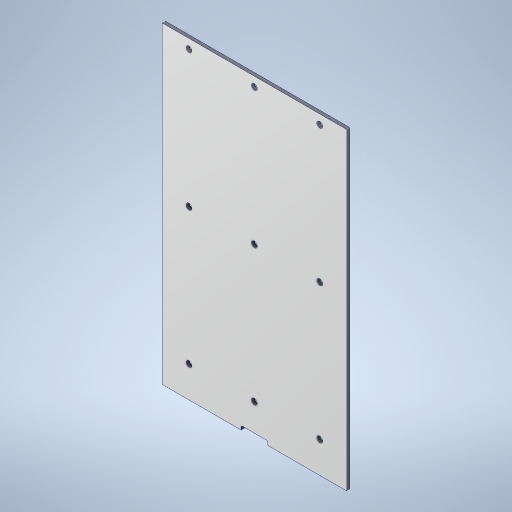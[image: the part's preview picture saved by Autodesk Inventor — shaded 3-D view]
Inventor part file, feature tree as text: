
AUTODESK INVENTOR PART (.ipt)
format: ipt  version: 2024 (Build 280153000, 153)  size: 298,496 bytes
history: native  units: mm
features: extrude x4, sketch x3, other x2, hole x1
ambient origin geometry x8: Origin, YZ Plane, XZ Plane, XY Plane, X Axis, Y Axis, Z Axis, Center Point
bodies: Body1 (feature_tree), Body2 (feature_tree)
feature tree (10):
  other  "Laminate"
  sketch  "Sketch1"  dims[d0=169.5mm d1=287.25mm]
  extrude  "Extrusion1"  Depth=287.25mm
  extrude  "Extrusion2"  Depth=2.9mm TaperAngle=0.0deg
  extrude  "Extrusion3"  Depth=1.0mm
  hole  "Hole1"  [1 undecoded]
  extrude  "Extrusion4"  Depth=10.0mm
  other  "Core"
  sketch  "Sketch2"  dims[d2=3.0mm d3=0.0mm d4=2.9mm d5=0.0mm]
  sketch  "Sketch3"  dims[d6=2.9mm d7=0.0mm d12=5.4mm d13=6.0mm d14=4.0mm d15=2.0mm d16=90.0deg d17=8.0mm d18=20.594885mm d19=250.0mm d20=120.0mm d22=10.0mm d23=24.0mm d24=3.625mm d25=0.0mm d26=0.0mm d27=1.0mm]
note: 1 required parameter value undecoded (feature->parameter linkage not recoverable at this tier; creation-order binding heuristic only, values carry confidence <= 0.55)
